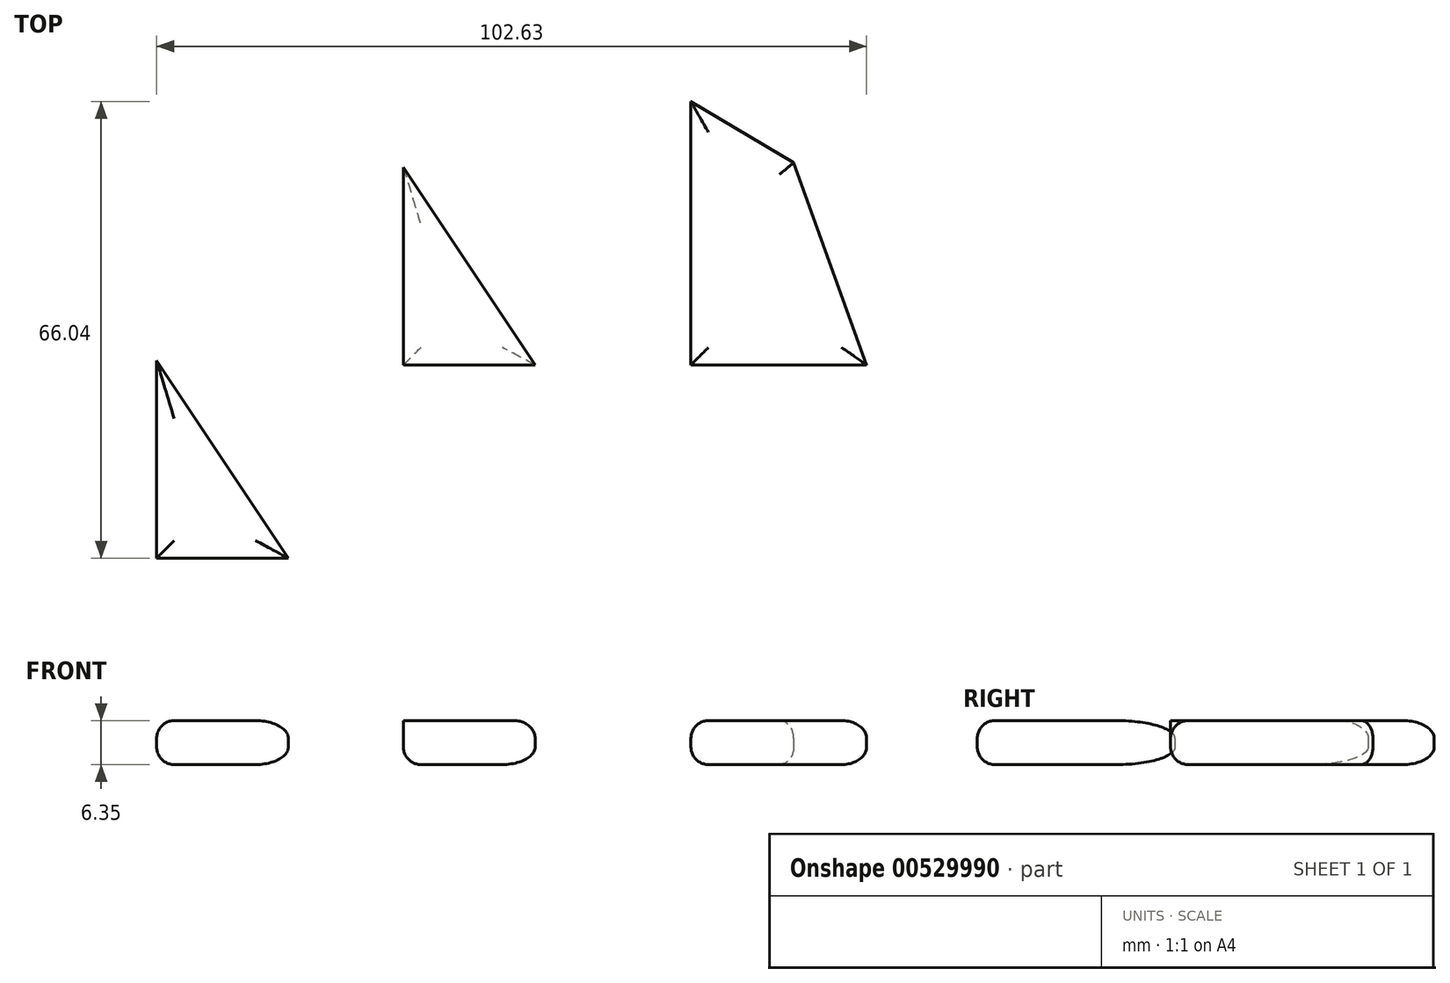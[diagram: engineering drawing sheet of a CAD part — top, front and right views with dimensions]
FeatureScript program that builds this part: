
annotation { "Feature Type Name" : "Feature", "Feature Type Description" : "" }
export const myFeature = defineFeature(function(context is Context, id is Id, definition is map)
    precondition{}
    {
        {
            var Q0;
            Q0=qCreatedBy(makeId("Top.planeOp"),FACE);
            var sketch = newSketch(context, id + "F0", { "sketchPlane" : qUnion([Q0])});
            skLineSegment(sketch, "E0", {"start": v(0, 0) * mm, "end": v(25.4, 0) * mm});
            skLineSegment(sketch, "E1", {"start": v(0, 0) * mm, "end": v(0, 38.1) * mm});
            skLineSegment(sketch, "E2", {"start": v(0, 38.1) * mm, "end": v(14.86, 29.25) * mm});
            skLineSegment(sketch, "E3", {"start": v(14.86, 29.25) * mm, "end": v(25.4, 0) * mm});
            skSolve(sketch);
        }
        {
            var Q0;
            Q0=makeQuery(id+"F0.imprint","IMPRINT",FACE,{"disambiguationData":[TD([[makeQuery(id+"F0.imprint","IMPRINT",EDGE,{"derivedFrom":sQuery(id+"F0.wireOp",EDGE,"E0")}),1.0]])]});
            extrude(context, id + "F1", {"entities" : qUnion([Q0]), "depth" : 6.35 * mm, "offsetDistance" : 25.4 * mm});
        }
        {
            var Q0;
            Q0=makeQuery(id+"F1.opExtrude","CAP_FACE",FACE,{"disambiguationData":[OSD([sQuery(id+"F0.wireOp",EDGE,"E0"),sQuery(id+"F0.wireOp",EDGE,"E1"),sQuery(id+"F0.wireOp",EDGE,"E2"),sQuery(id+"F0.wireOp",EDGE,"E3")])],"isStart":false});
            var Q1;
            Q1=makeQuery(id+"F1.opExtrude","CAP_FACE",FACE,{"disambiguationData":[OSD([sQuery(id+"F0.wireOp",EDGE,"E0"),sQuery(id+"F0.wireOp",EDGE,"E1"),sQuery(id+"F0.wireOp",EDGE,"E2"),sQuery(id+"F0.wireOp",EDGE,"E3")])],"isStart":true});
            fillet(context, id + "F2", {"entities" : qUnion([Q0, Q1]), "radius" : 2.54 * mm, "tangentPropagation" : true, "allowEdgeOverflow" : false});
        }
        {
            var Q0;
            Q0=qCreatedBy(makeId("Top.planeOp"),FACE);
            var sketch = newSketch(context, id + "F3", { "sketchPlane" : qUnion([Q0])});
            skLineSegment(sketch, "E4", {"start": v(-41.56, 0) * mm, "end": v(-22.51, 0) * mm});
            skLineSegment(sketch, "E5", {"start": v(-41.56, 0) * mm, "end": v(-41.56, 28.57) * mm});
            skLineSegment(sketch, "E6", {"start": v(-41.56, 28.58) * mm, "end": v(-22.51, 0) * mm});
            skLineSegment(sketch, "E7", {"start": v(-77.23, -27.94) * mm, "end": v(-58.18, -27.94) * mm});
            skLineSegment(sketch, "E8", {"start": v(-77.23, -27.94) * mm, "end": v(-77.23, 0.63) * mm});
            skLineSegment(sketch, "E9", {"start": v(-77.23, 0.63) * mm, "end": v(-58.18, -27.94) * mm});
            skSolve(sketch);
        }
        {
            var Q0;
            Q0=makeQuery(id+"F3.imprint","IMPRINT",FACE,{"disambiguationData":[TD([[makeQuery(id+"F3.imprint","IMPRINT",EDGE,{"derivedFrom":sQuery(id+"F3.wireOp",EDGE,"E4")}),1.0]])]});
            var Q1;
            Q1=makeQuery(id+"F3.imprint","IMPRINT",FACE,{"disambiguationData":[TD([[makeQuery(id+"F3.imprint","IMPRINT",EDGE,{"derivedFrom":sQuery(id+"F3.wireOp",EDGE,"E7")}),1.0]])]});
            extrude(context, id + "F4", {"entities" : qUnion([Q0, Q1]), "depth" : 6.35 * mm, "offsetDistance" : 25.4 * mm});
        }
        {
            var Q0;
            Q0=makeQuery(id+"F4.opExtrude","CAP_FACE",FACE,{"disambiguationData":[OSD([sQuery(id+"F3.wireOp",EDGE,"E7"),sQuery(id+"F3.wireOp",EDGE,"E8"),sQuery(id+"F3.wireOp",EDGE,"E9")])],"isStart":false});
            var Q1;
            Q1=makeQuery(id+"F4.opExtrude","CAP_EDGE",EDGE,{"disambiguationData":[OSD([sQuery(id+"F3.wireOp",EDGE,"E6")])],"isStart":false});
            var Q2;
            Q2=makeQuery(id+"F4.opExtrude","CAP_EDGE",EDGE,{"disambiguationData":[OSD([sQuery(id+"F3.wireOp",EDGE,"E9")])],"isStart":true});
            var Q3;
            Q3=makeQuery(id+"F4.opExtrude","CAP_EDGE",EDGE,{"disambiguationData":[OSD([sQuery(id+"F3.wireOp",EDGE,"E6")])],"isStart":true});
            var Q4;
            Q4=makeQuery(id+"F4.opExtrude","CAP_EDGE",EDGE,{"disambiguationData":[OSD([sQuery(id+"F3.wireOp",EDGE,"E4")])],"isStart":true});
            var Q5;
            Q5=makeQuery(id+"F4.opExtrude","CAP_EDGE",EDGE,{"disambiguationData":[OSD([sQuery(id+"F3.wireOp",EDGE,"E8")])],"isStart":true});
            var Q6;
            Q6=makeQuery(id+"F4.opExtrude","CAP_EDGE",EDGE,{"disambiguationData":[OSD([sQuery(id+"F3.wireOp",EDGE,"E7")])],"isStart":true});
            var Q7;
            Q7=makeQuery(id+"F4.opExtrude","CAP_EDGE",EDGE,{"disambiguationData":[OSD([sQuery(id+"F3.wireOp",EDGE,"E5")])],"isStart":true});
            fillet(context, id + "F5", {"entities" : qUnion([Q0, Q1, Q2, Q3, Q4, Q5, Q6, Q7]), "radius" : 2.54 * mm, "tangentPropagation" : true, "allowEdgeOverflow" : false});
        }
    });
